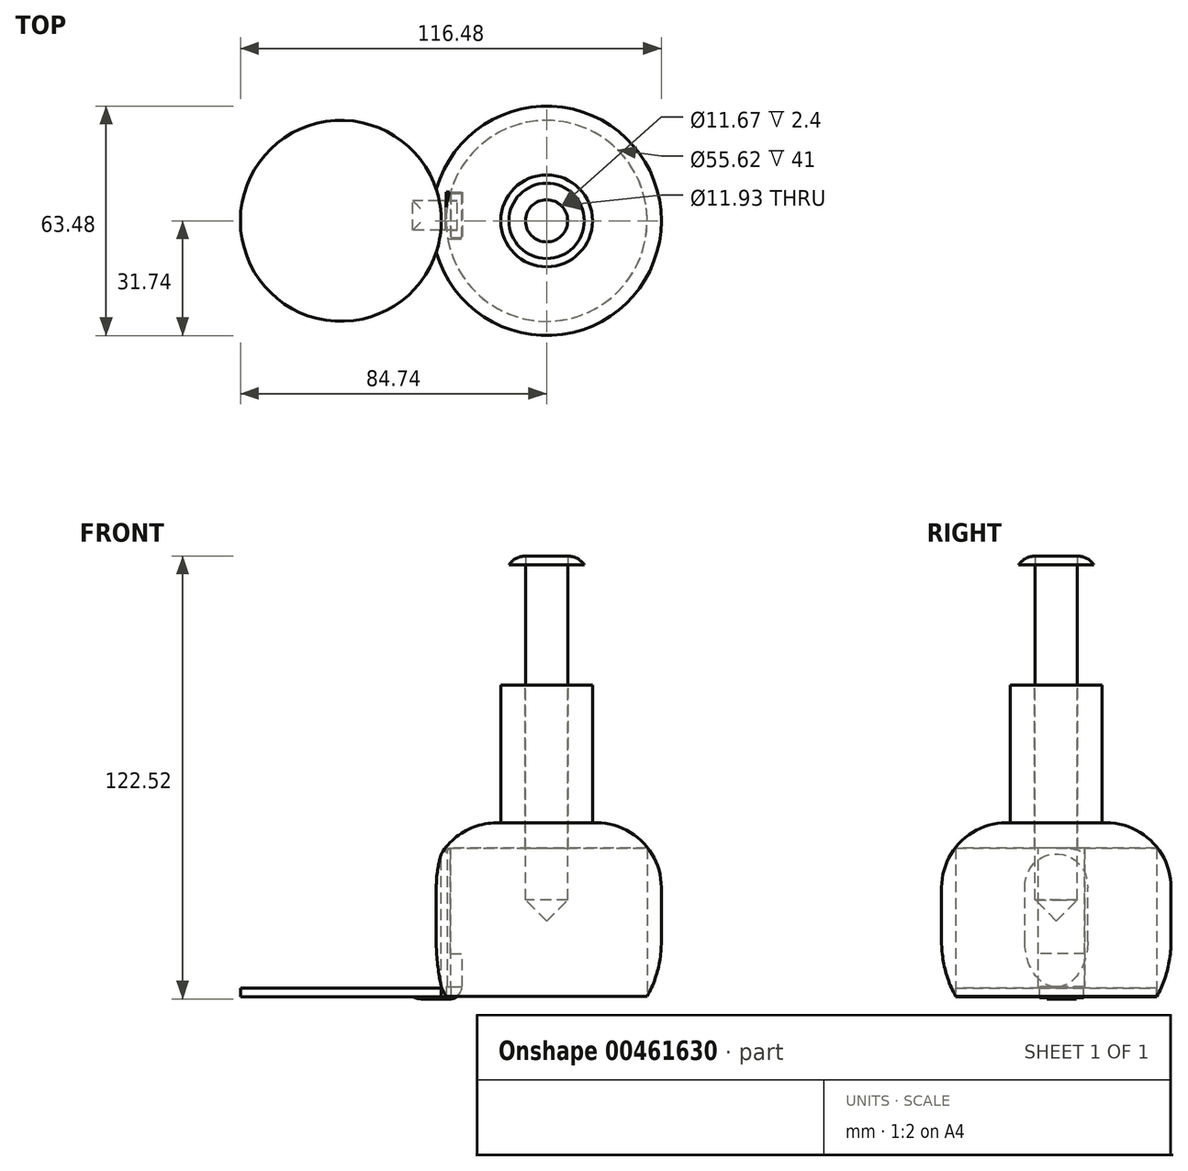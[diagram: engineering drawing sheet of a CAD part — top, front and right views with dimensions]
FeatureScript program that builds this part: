
annotation { "Feature Type Name" : "Feature", "Feature Type Description" : "" }
export const myFeature = defineFeature(function(context is Context, id is Id, definition is map)
    precondition{}
    {
        {
            var Q0;
            Q0=qCreatedBy(makeId("Top.planeOp"),FACE);
            var sketch = newSketch(context, id + "F0", { "sketchPlane" : qUnion([Q0])});
            skCircle(sketch, "E0", {"center": v(0, 0) * mm, "radius": 12.7 * mm});
            skSolve(sketch);
        }
        {
            var Q0;
            Q0=makeQuery(id+"F0.imprint","IMPRINT",FACE,{"disambiguationData":[TD([[makeQuery(id+"F0.imprint","IMPRINT",EDGE,{"derivedFrom":sQuery(id+"F0.wireOp",EDGE,"E0")}),1.0]])]});
            extrude(context, id + "F1", {"entities" : qUnion([Q0]), "depth" : 38.1 * mm});
        }
        {
            var Q0;
            Q0=makeQuery(id+"F1.opExtrude","CAP_FACE",FACE,{"disambiguationData":[OSD([sQuery(id+"F0.wireOp",EDGE,"E0")])],"isStart":false});
            var sketch = newSketch(context, id + "F2", { "sketchPlane" : qUnion([Q0])});
            skCircle(sketch, "E1", {"center": v(0, 0) * mm, "radius": 5.96 * mm});
            skSolve(sketch);
        }
        {
            var Q0;
            Q0=makeQuery(id+"F2.imprint","IMPRINT",FACE,{"disambiguationData":[TD([[makeQuery(id+"F2.imprint","IMPRINT",EDGE,{"derivedFrom":sQuery(id+"F2.wireOp",EDGE,"E1")}),1.0]])]});
            extrude(context, id + "F3", {"entities" : qUnion([Q0]), "operationType" : NewBodyOperationType.REMOVE, "endBound" : BoundingType.THROUGH_ALL, "oppositeDirection" : true, "depth" : 25 * mm});
        }
        {
            var Q0;
            Q0=qCreatedBy(makeId("Top.planeOp"),FACE);
            var sketch = newSketch(context, id + "F4", { "sketchPlane" : qUnion([Q0])});
            skCircle(sketch, "E2", {"center": v(0, 0) * mm, "radius": 31.74 * mm});
            skSolve(sketch);
        }
        {
            var Q0;
            Q0=makeQuery(id+"F4.imprint","IMPRINT",FACE,{"disambiguationData":[TD([[makeQuery(id+"F4.imprint","IMPRINT",EDGE,{"derivedFrom":sQuery(id+"F4.wireOp",EDGE,"E2")}),1.0]])]});
            extrude(context, id + "F5", {"entities" : qUnion([Q0]), "operationType" : NewBodyOperationType.ADD, "oppositeDirection" : true, "depth" : 23 * mm});
        }
        {
            var Q0;
            Q0=makeQuery(id+"F5.opExtrude","CAP_FACE",FACE,{"disambiguationData":[OSD([sQuery(id+"F4.wireOp",EDGE,"E2")])],"isStart":false});
            extrude(context, id + "F6", {"entities" : qUnion([Q0]), "operationType" : NewBodyOperationType.ADD, "depth" : 25 * mm});
        }
        {
            var Q0;
            Q0=makeQuery(id+"F6.opExtrude","CAP_FACE",FACE,{"disambiguationData":[OSD([sQuery(id+"F4.wireOp",EDGE,"E2")])],"isStart":false});
            var sketch = newSketch(context, id + "F7", { "sketchPlane" : qUnion([Q0])});
            skCircle(sketch, "E3", {"center": v(0, 0) * mm, "radius": 27.8 * mm});
            skSolve(sketch);
        }
        {
            var Q0;
            Q0=makeQuery(id+"F7.imprint","IMPRINT",FACE,{"disambiguationData":[TD([[makeQuery(id+"F7.imprint","IMPRINT",EDGE,{"derivedFrom":sQuery(id+"F7.wireOp",EDGE,"E3")}),1.0]])]});
            extrude(context, id + "F8", {"entities" : qUnion([Q0]), "operationType" : NewBodyOperationType.REMOVE, "oppositeDirection" : true, "depth" : 41 * mm});
        }
        {
            var Q0;
            Q0=makeQuery(id+"F5.boolean.opBoolean","SPLIT",FACE,{"disambiguationData":[TD([makeQuery(id+"F3.boolean.opBoolean","COPY",FACE,{"derivedFrom":makeQuery(id+"F3.opExtrude","SWEPT_FACE",FACE,{"disambiguationData":[OSD([sQuery(id+"F2.wireOp",EDGE,"E1")])]})})])],"derivedFrom":makeQuery(id+"F5.opExtrude","CAP_FACE",FACE,{"disambiguationData":[OSD([sQuery(id+"F4.wireOp",EDGE,"E2")])],"isStart":true})});
            extrude(context, id + "F9", {"entities" : qUnion([Q0]), "operationType" : NewBodyOperationType.REMOVE, "oppositeDirection" : true, "depth" : 49 * mm});
        }
        {
            var Q0;
            Q0=makeQuery(id+"F5.opExtrude","CAP_EDGE",EDGE,{"disambiguationData":[OSD([sQuery(id+"F4.wireOp",EDGE,"E2")])],"isStart":true});
            fillet(context, id + "F10", {"entities" : qUnion([Q0]), "radius" : 17.87 * mm, "tangentPropagation" : true, "allowEdgeOverflow" : false});
        }
        {
            var Q0;
            Q0=makeQuery(id+"F6.opExtrude","CAP_EDGE",EDGE,{"disambiguationData":[OSD([sQuery(id+"F4.wireOp",EDGE,"E2")])],"isStart":false});
            fillet(context, id + "F11", {"entities" : qUnion([Q0]), "radius" : 31.14 * mm, "tangentPropagation" : true, "allowEdgeOverflow" : false});
        }
        {
            var Q0;
            Q0=makeQuery(id+"F8.boolean.opBoolean","COPY",FACE,{"derivedFrom":makeQuery(id+"F8.opExtrude","CAP_FACE",FACE,{"disambiguationData":[OSD([sQuery(id+"F7.wireOp",EDGE,"E3")])],"isStart":false})});
            var sketch = newSketch(context, id + "F12", { "sketchPlane" : qUnion([Q0])});
            skLineSegment(sketch, "E4.bottom", {"start": v(-27.8, 0) * mm, "end": v(-23.3, 0) * mm});
            skLineSegment(sketch, "E4.top", {"start": v(-27.8, 4.98) * mm, "end": v(-23.3, 4.98) * mm});
            skLineSegment(sketch, "E4.left", {"start": v(-27.8, 0) * mm, "end": v(-27.8, 4.98) * mm});
            skLineSegment(sketch, "E4.right", {"start": v(-23.3, 0) * mm, "end": v(-23.3, 4.98) * mm});
            skSolve(sketch);
        }
        {
            var Q0;
            {var subQ0=sQuery(id+"F12.wireOp",EDGE,"E4.bottom");Q0=makeQuery(id+"F12.imprint","IMPRINT",FACE,{"disambiguationData":[TD([[makeQuery(id+"F12.imprint","IMPRINT",EDGE,{"derivedFrom":subQ0}),1.0]])]});}
            extrude(context, id + "F13", {"entities" : qUnion([Q0]), "operationType" : NewBodyOperationType.ADD, "depth" : 38.3 * mm});
        }
        {
            var Q0;
            Q0=makeQuery(id+"F13.opExtrude","SWEPT_FACE",FACE,{"disambiguationData":[OSD([sQuery(id+"F12.wireOp",EDGE,"E4.bottom")])]});
            extrude(context, id + "F14", {"entities" : qUnion([Q0]), "operationType" : NewBodyOperationType.ADD, "depth" : 7.9 * mm});
        }
        {
            var Q0;
            {var subQ0=sQuery(id+"F12.wireOp",EDGE,"E4.right");Q0=makeQuery(id+"F14.boolean.opBoolean","MERGE",FACE,{"derivedFrom":[makeQuery(id+"F13.opExtrude","SWEPT_FACE",FACE,{"disambiguationData":[OSD([subQ0])]}),makeQuery(id+"F14.opExtrude","SWEPT_FACE",FACE,{"disambiguationData":[OSD([sQuery(id+"F12.wireOp",EDGE,"E4.bottom"),subQ0])]})]});}
            var sketch = newSketch(context, id + "F15", { "sketchPlane" : qUnion([Q0])});
            skLineSegment(sketch, "E5.bottom", {"start": v(7.9, -36.2) * mm, "end": v(-4.98, -36.2) * mm});
            skLineSegment(sketch, "E5.top", {"start": v(7.9, -7) * mm, "end": v(-4.98, -7) * mm});
            skLineSegment(sketch, "E5.left", {"start": v(7.9, -36.2) * mm, "end": v(7.9, -7) * mm});
            skLineSegment(sketch, "E5.right", {"start": v(-4.98, -36.2) * mm, "end": v(-4.98, -7) * mm});
            skSolve(sketch);
        }
        {
            var Q0;
            Q0=makeQuery(id+"F15.imprint","IMPRINT",FACE,{"disambiguationData":[TD([[makeQuery(id+"F15.imprint","IMPRINT",EDGE,{"derivedFrom":sQuery(id+"F15.wireOp",EDGE,"E5.bottom")}),-1.0]])]});
            extrude(context, id + "F16", {"entities" : qUnion([Q0]), "operationType" : NewBodyOperationType.REMOVE, "oppositeDirection" : true, "depth" : 3.3 * mm});
        }
        {
            var Q0;
            {var subQ0=sQuery(id+"F12.wireOp",EDGE,"E4.bottom");Q0=makeQuery(id+"F14.boolean.opBoolean","MERGE",FACE,{"derivedFrom":[makeQuery(id+"F13.opExtrude","CAP_FACE",FACE,{"disambiguationData":[OSD([sQuery(id+"F7.wireOp",EDGE,"E3"),subQ0,sQuery(id+"F12.wireOp",EDGE,"E4.top"),sQuery(id+"F12.wireOp",EDGE,"E4.right")])],"isStart":false}),makeQuery(id+"F14.opExtrude","SWEPT_FACE",FACE,{"disambiguationData":[OSD([subQ0]),TDD([makeQuery(id+"F13.opExtrude","CAP_EDGE",EDGE,{"disambiguationData":[OSD([subQ0])],"isStart":false})])]})]});}
            var sketch = newSketch(context, id + "F17", { "sketchPlane" : qUnion([Q0])});
            skLineSegment(sketch, "E6.bottom", {"start": v(-26.38, 4.66) * mm, "end": v(-24.65, 4.66) * mm});
            skLineSegment(sketch, "E6.top", {"start": v(-26.38, -7.52) * mm, "end": v(-24.65, -7.52) * mm});
            skLineSegment(sketch, "E6.left", {"start": v(-24.65, 4.66) * mm, "end": v(-24.65, -7.52) * mm});
            skLineSegment(sketch, "E6.right", {"start": v(-26.38, 4.66) * mm, "end": v(-26.38, -7.52) * mm});
            skSolve(sketch);
        }
        {
            var Q0;
            Q0=makeQuery(id+"F17.imprint","IMPRINT",FACE,{"disambiguationData":[TD([[makeQuery(id+"F17.imprint","IMPRINT",EDGE,{"derivedFrom":sQuery(id+"F17.wireOp",EDGE,"E6.bottom")}),-1.0]])]});
            extrude(context, id + "F18", {"entities" : qUnion([Q0]), "operationType" : NewBodyOperationType.ADD, "depth" : 3.1 * mm});
        }
        {
            var Q0;
            Q0=qCreatedBy(makeId("Top.planeOp"),FACE);
            var sketch = newSketch(context, id + "F19", { "sketchPlane" : qUnion([Q0])});
            skCircle(sketch, "E7", {"center": v(-56.94, 0) * mm, "radius": 27.8 * mm});
            skSolve(sketch);
        }
        {
            var Q0;
            Q0=makeQuery(id+"F19.imprint","IMPRINT",FACE,{"disambiguationData":[TD([[makeQuery(id+"F19.imprint","IMPRINT",EDGE,{"derivedFrom":sQuery(id+"F19.wireOp",EDGE,"E7")}),1.0]])]});
            extrude(context, id + "F20", {"entities" : qUnion([Q0]), "oppositeDirection" : true, "depth" : 48.1 * mm});
        }
        {
            var Q0;
            Q0=makeQuery(id+"F20.opExtrude","CAP_FACE",FACE,{"disambiguationData":[OSD([sQuery(id+"F19.wireOp",EDGE,"E7")])],"isStart":true});
            extrude(context, id + "F21", {"entities" : qUnion([Q0]), "operationType" : NewBodyOperationType.REMOVE, "oppositeDirection" : true, "depth" : 45.7 * mm});
        }
        {
            var Q0;
            Q0=makeQuery(id+"F20.opExtrude","CAP_FACE",FACE,{"disambiguationData":[OSD([sQuery(id+"F19.wireOp",EDGE,"E7")])],"isStart":false});
            var sketch = newSketch(context, id + "F22", { "sketchPlane" : qUnion([Q0])});
            skLineSegment(sketch, "E8.bottom", {"start": v(-28.05, 2.6) * mm, "end": v(-37.05, 2.6) * mm});
            skLineSegment(sketch, "E8.top", {"start": v(-28.05, -5.6) * mm, "end": v(-37.05, -5.6) * mm});
            skLineSegment(sketch, "E8.left", {"start": v(-28.05, 2.6) * mm, "end": v(-28.05, -5.6) * mm});
            skLineSegment(sketch, "E8.right", {"start": v(-37.05, 2.6) * mm, "end": v(-37.05, -5.6) * mm});
            skSolve(sketch);
        }
        {
            var Q0;
            {var subQ0=sQuery(id+"F22.wireOp",EDGE,"E8.right");Q0=makeQuery(id+"F22.imprint","IMPRINT",FACE,{"disambiguationData":[TD([[makeQuery(id+"F22.imprint","IMPRINT",EDGE,{"derivedFrom":subQ0}),1.0]])]});}
            var Q1;
            {var subQ0=sQuery(id+"F22.wireOp",EDGE,"E8.left");Q1=makeQuery(id+"F22.imprint","IMPRINT",FACE,{"disambiguationData":[TD([[makeQuery(id+"F22.imprint","IMPRINT",EDGE,{"derivedFrom":subQ0}),-1.0]])]});}
            extrude(context, id + "F23", {"entities" : qUnion([Q0, Q1]), "operationType" : NewBodyOperationType.ADD, "depth" : 0.6 * mm});
        }
        {
            var Q0;
            Q0=qCreatedBy(makeId("Top.planeOp"),FACE);
            var sketch = newSketch(context, id + "F24", { "sketchPlane" : qUnion([Q0])});
            skCircle(sketch, "E9", {"center": v(0, 0) * mm, "radius": 5.84 * mm});
            skSolve(sketch);
        }
        {
            var Q0;
            Q0=makeQuery(id+"F24.imprint","IMPRINT",FACE,{"disambiguationData":[TD([[makeQuery(id+"F24.imprint","IMPRINT",EDGE,{"derivedFrom":sQuery(id+"F24.wireOp",EDGE,"E9")}),1.0]])]});
            extrude(context, id + "F25", {"entities" : qUnion([Q0]), "oppositeDirection" : true, "depth" : 27.1 * mm});
        }
        {
            var Q0;
            Q0=makeQuery(id+"F25.opExtrude","CAP_FACE",FACE,{"disambiguationData":[OSD([sQuery(id+"F24.wireOp",EDGE,"E9")])],"isStart":true});
            extrude(context, id + "F26", {"entities" : qUnion([Q0]), "operationType" : NewBodyOperationType.ADD, "depth" : 71.4 * mm});
        }
        {
            var Q0;
            Q0=makeQuery(id+"F26.opExtrude","CAP_FACE",FACE,{"disambiguationData":[OSD([sQuery(id+"F24.wireOp",EDGE,"E9")])],"isStart":false});
            var sketch = newSketch(context, id + "F27", { "sketchPlane" : qUnion([Q0])});
            skCircle(sketch, "E10", {"center": v(0, 0) * mm, "radius": 10.42 * mm});
            skSolve(sketch);
        }
        {
            var Q0;
            Q0=makeQuery(id+"F27.imprint","IMPRINT",FACE,{"disambiguationData":[TD([[makeQuery(id+"F27.imprint","IMPRINT",EDGE,{"derivedFrom":sQuery(id+"F27.wireOp",EDGE,"E10")}),1.0]])]});
            extrude(context, id + "F28", {"entities" : qUnion([Q0]), "depth" : 2.4 * mm});
        }
        {
            var Q0;
            Q0=makeQuery(id+"F26.opExtrude","CAP_FACE",FACE,{"disambiguationData":[OSD([sQuery(id+"F24.wireOp",EDGE,"E9")])],"isStart":false});
            extrude(context, id + "F29", {"entities" : qUnion([Q0]), "depth" : 2.6 * mm});
        }
        {
            var Q0;
            Q0=makeQuery(id+"F23.opExtrude","SWEPT_FACE",FACE,{"disambiguationData":[OSD([sQuery(id+"F22.wireOp",EDGE,"E8.left")])]});
            extrude(context, id + "F30", {"entities" : qUnion([Q0]), "depth" : 3.3 * mm});
        }
        {
            var Q0;
            Q0=makeQuery(id+"F18.opExtrude","SWEPT_FACE",FACE,{"disambiguationData":[OSD([sQuery(id+"F17.wireOp",EDGE,"E6.left")])]});
            extrude(context, id + "F31", {"entities" : qUnion([Q0]), "operationType" : NewBodyOperationType.ADD, "depth" : 1.2 * mm});
        }
        {
            var Q0;
            {var subQ0=sQuery(id+"F17.wireOp",EDGE,"E6.left");Q0=makeQuery(id+"F31.opExtrude","CAP_EDGE",EDGE,{"disambiguationData":[OSD([subQ0]),TDD([makeQuery(id+"F18.opExtrude","CAP_EDGE",EDGE,{"disambiguationData":[OSD([subQ0])],"isStart":false})])],"isStart":false});}
            var Q1;
            {var subQ0=sQuery(id+"F22.wireOp",EDGE,"E8.left");Q1=makeQuery(id+"F30.opExtrude","CAP_EDGE",EDGE,{"disambiguationData":[OSD([subQ0]),TDD([makeQuery(id+"F23.opExtrude","CAP_EDGE",EDGE,{"disambiguationData":[OSD([subQ0])],"isStart":false})])],"isStart":false});}
            fillet(context, id + "F32", {"entities" : qUnion([Q0, Q1]), "radius" : 3.14 * mm, "tangentPropagation" : true, "allowEdgeOverflow" : false});
        }
        {
            var Q0;
            Q0=makeQuery(id+"F25.opExtrude","CAP_FACE",FACE,{"disambiguationData":[OSD([sQuery(id+"F24.wireOp",EDGE,"E9")])],"isStart":false});
            chamfer(context, id + "F33", {"entities" : qUnion([Q0]), "width" : 5.83 * mm, "tangentPropagation" : true});
        }
        {
            var Q0;
            Q0=makeQuery(id+"F28.opExtrude","CAP_EDGE",EDGE,{"disambiguationData":[OSD([sQuery(id+"F27.wireOp",EDGE,"E10")])],"isStart":false});
            fillet(context, id + "F34", {"entities" : qUnion([Q0]), "radius" : 5.55 * mm, "tangentPropagation" : true, "allowEdgeOverflow" : false});
        }
        {
            var Q0;
            Q0=makeQuery(id+"F29.opExtrude","CAP_FACE",FACE,{"disambiguationData":[OSD([sQuery(id+"F24.wireOp",EDGE,"E9")])],"isStart":false});
            extrude(context, id + "F35", {"entities" : qUnion([Q0]), "operationType" : NewBodyOperationType.REMOVE, "oppositeDirection" : true, "depth" : 0.18 * mm});
        }
        {
            var Q0;
            Q0=makeQuery(id+"F23.opExtrude","CAP_EDGE",EDGE,{"disambiguationData":[OSD([sQuery(id+"F22.wireOp",EDGE,"E8.top")])],"isStart":false});
            var Q1;
            Q1=makeQuery(id+"F23.opExtrude","CAP_EDGE",EDGE,{"disambiguationData":[OSD([sQuery(id+"F22.wireOp",EDGE,"E8.right")])],"isStart":false});
            var Q2;
            Q2=makeQuery(id+"F23.opExtrude","CAP_EDGE",EDGE,{"disambiguationData":[OSD([sQuery(id+"F22.wireOp",EDGE,"E8.bottom")])],"isStart":false});
            fillet(context, id + "F36", {"entities" : qUnion([Q0, Q1, Q2]), "radius" : 5.96 * mm, "tangentPropagation" : true, "allowEdgeOverflow" : false});
        }
    });
